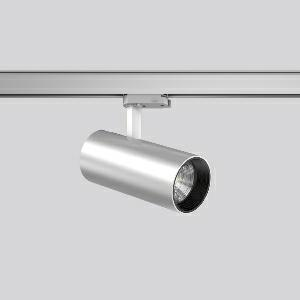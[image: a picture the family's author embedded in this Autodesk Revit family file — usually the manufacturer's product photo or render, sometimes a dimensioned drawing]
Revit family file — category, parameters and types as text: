
# Revit family: deecos_s_mini_742207_004_2_76_ea6a
name_source: partatom
category: Lighting Fixtures
units: mm (PartAtom-declared; Revit-internal decimal feet)

## family parameters
Cut with Voids When Loaded = No
Host = Face
Light Source = No
Part Type = Normal
Room Calculation Point = No
Round Connector Dimension = Use Diameter
Shared = No

## types (1)
- DEECOS S mini (1 x LED Modul 927, 2850 lm, 2700)
    Apparent Load = 29 VA
    Approval mark = CE
    CIE Flux Codes = 96 100 100 100 100
    Color Rendering = 92
    Color Temperature = 2700
    Default Elevation = 1800 mm
    Description = Series: DEECOS S mini
LED surface-mounted projector in modern design with no visible cooling ribs. Housing: die-cast aluminium, powder-coated. Rotation range: 356°. Swivel range: 90°. Black plastic ring and recessed LED to prevent glare from the side. Optical assembly with lens made of plastic (polycarbonate) for the best homogeneous light distribution - can be changed without tools. Best colour rendering index Ra>90. With adapter for RZB 3-circuit DALI tracks. Suitable for Track on ceiling, Wall track. High quality converter without flickering and stroboscopic effect. The following accessories can be mounted without use of tools: interchangeable lenses, decorative glasses, honeycomb louvre, clear and frosted diffusers, white interchangeable plastic ring. 
Colour: silver
Diameter: 87 mm
Height: 214 mm
Lamp: LED
Socket: without socket
Colour temperature: 2700K
Colour rendering index (CRI): 92
System power: 29 W
Rated luminous flux: 2850 lm
Luminous efficiency: 98 lm/W
Control gear: Converter, dimmable, DALI
Protection class: I
Type of protection: IP 20
    Height = 214 mm
    Lamp = 1 x LED Modul 927
    Lamp Light Flux = 2850 lm
    Lamp count = 1
    Length = 87 mm
    Lifetime = 50000 h
    Luminous efficacy = 98 lm/W
    Manufacturer = RZB
    ModVariant = No
    Model = 742207.004.2.76
    Mounting Place = Ceiling
    Mounting Type = Rail mounted
    Number of Poles = 1
    OnlyDefault = Yes
    Power Factor = 1
    Product Name = DEECOS S mini
    Product group = Track mounted projectors
    ProductGroupID = 301
    Protection Class = Protection class I
    Protection Degree = IP 20
    RLX_Detail_Level = 1
    RLX_Emergency_Light_Flux = 0 lm
    RLX_Emergency_Type = 0
    RLX_Emergency_Type_DB = No
    RlxData = <blob elided: 36821 chars, md5=5000f945>
    Socket = socket
    Standby Power = 0 W
    System Light Flux = 2850 lm
    System Power = 29 W
    Type Comments = Product without accessories
    Type Image = 741930.004.jpg
    URL = http://relux.com
    VarID = ---
    Voltage = 230 V
    Voltage Range = 220-240 V
    Weight = 0.00 kg
    Width = 0 mm  [stored 0 ft]

note: [stored X ft] marks values corroborated as IEEE doubles in the binary element streams (Revit-internal decimal feet)

## geometry (parser evidence)
native form markers: Blend x4, Sweep x11
no freeform markers — native parametric forms only
